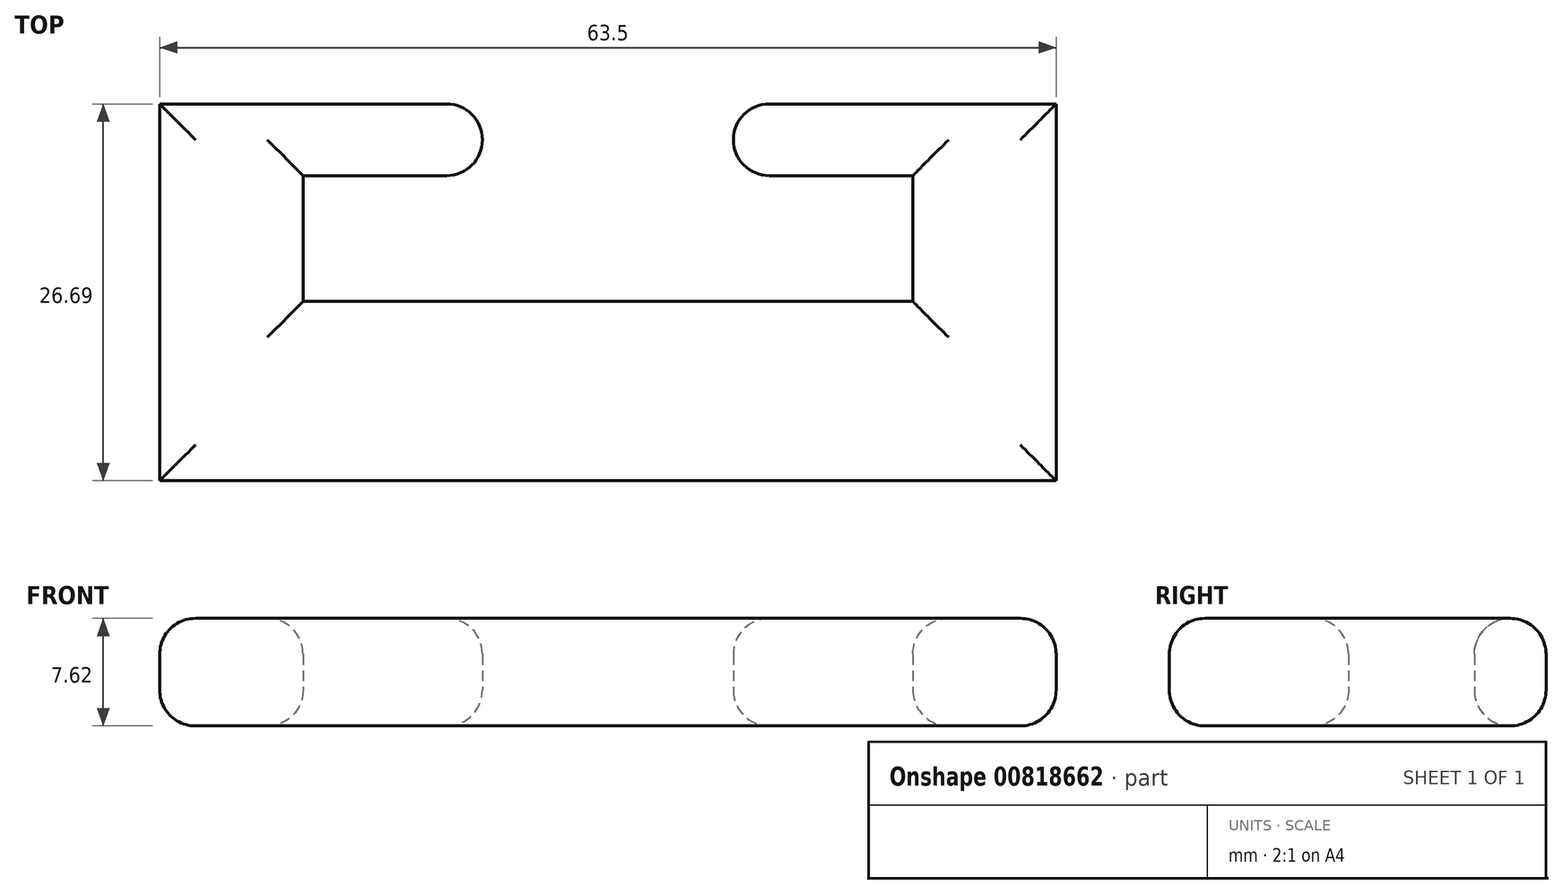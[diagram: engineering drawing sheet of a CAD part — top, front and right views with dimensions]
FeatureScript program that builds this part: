
annotation { "Feature Type Name" : "Feature", "Feature Type Description" : "" }
export const myFeature = defineFeature(function(context is Context, id is Id, definition is map)
    precondition{}
    {
        {
            var Q0;
            Q0=qCreatedBy(makeId("Top.planeOp"),FACE);
            var sketch = newSketch(context, id + "F0", { "sketchPlane" : qUnion([Q0])});
            skLineSegment(sketch, "E0.bottom", {"start": v(-30.15, 5.94) * mm, "end": v(33.35, 5.94) * mm});
            skLineSegment(sketch, "E0.top", {"start": v(-30.15, -6.76) * mm, "end": v(33.35, -6.76) * mm});
            skLineSegment(sketch, "E0.left", {"start": v(-30.15, 5.94) * mm, "end": v(-30.15, -6.76) * mm});
            skLineSegment(sketch, "E0.right", {"start": v(33.35, 5.94) * mm, "end": v(33.35, -6.76) * mm});
            skLineSegment(sketch, "E1.bottom", {"start": v(-30.15, 5.94) * mm, "end": v(-20, 5.94) * mm});
            skLineSegment(sketch, "E1.top", {"start": v(-30.15, 19.93) * mm, "end": v(-20, 19.93) * mm});
            skLineSegment(sketch, "E1.left", {"start": v(-30.15, 5.94) * mm, "end": v(-30.15, 19.93) * mm});
            skLineSegment(sketch, "E1.right", {"start": v(-20, 5.94) * mm, "end": v(-20, 19.93) * mm});
            skLineSegment(sketch, "E2.bottom", {"start": v(33.35, 5.94) * mm, "end": v(23.19, 5.94) * mm});
            skLineSegment(sketch, "E2.top", {"start": v(33.35, 19.93) * mm, "end": v(23.19, 19.93) * mm});
            skLineSegment(sketch, "E2.left", {"start": v(33.35, 5.94) * mm, "end": v(33.35, 19.93) * mm});
            skLineSegment(sketch, "E2.right", {"start": v(23.19, 5.94) * mm, "end": v(23.19, 19.93) * mm});
            skLineSegment(sketch, "E3.bottom", {"start": v(-20, 19.93) * mm, "end": v(-7.3, 19.93) * mm});
            skLineSegment(sketch, "E3.top", {"start": v(-20, 14.85) * mm, "end": v(-7.3, 14.85) * mm});
            skLineSegment(sketch, "E3.left", {"start": v(-20, 19.93) * mm, "end": v(-20, 14.85) * mm});
            skLineSegment(sketch, "E3.right", {"start": v(-7.3, 19.93) * mm, "end": v(-7.3, 14.85) * mm});
            skLineSegment(sketch, "E4.bottom", {"start": v(23.19, 19.93) * mm, "end": v(10.49, 19.93) * mm});
            skLineSegment(sketch, "E4.top", {"start": v(23.19, 14.85) * mm, "end": v(10.49, 14.85) * mm});
            skLineSegment(sketch, "E4.left", {"start": v(23.19, 19.93) * mm, "end": v(23.19, 14.85) * mm});
            skLineSegment(sketch, "E4.right", {"start": v(10.49, 19.93) * mm, "end": v(10.49, 14.85) * mm});
            skSolve(sketch);
        }
        {
            var Q0;
            Q0 = qSketchRegion(id + "F0", true);
            extrude(context, id + "F1", {"entities" : qUnion([Q0]), "depth" : 7.62 * mm, "offsetDistance" : 25.4 * mm});
        }
        {
            var Q0;
            Q0=makeQuery(id+"F1.opExtrude","CAP_EDGE",EDGE,{"disambiguationData":[OSD([sQuery(id+"F0.wireOp",EDGE,"E0.top")])],"isStart":false});
            var Q1;
            Q1=makeQuery(id+"F1.opExtrude","CAP_EDGE",EDGE,{"disambiguationData":[OSD([sQuery(id+"F0.wireOp",EDGE,"E0.bottom")])],"isStart":false});
            var Q2;
            Q2=makeQuery(id+"F1.opExtrude","CAP_EDGE",EDGE,{"disambiguationData":[OSD([sQuery(id+"F0.wireOp",EDGE,"E0.left"),sQuery(id+"F0.wireOp",EDGE,"E1.left")])],"isStart":false});
            var Q3;
            Q3=makeQuery(id+"F1.opExtrude","CAP_EDGE",EDGE,{"disambiguationData":[OSD([sQuery(id+"F0.wireOp",EDGE,"E0.right"),sQuery(id+"F0.wireOp",EDGE,"E2.left")])],"isStart":false});
            var Q4;
            Q4=makeQuery(id+"F1.opExtrude","CAP_EDGE",EDGE,{"disambiguationData":[OSD([sQuery(id+"F0.wireOp",EDGE,"E2.top"),sQuery(id+"F0.wireOp",EDGE,"E4.bottom")])],"isStart":false});
            var Q5;
            Q5=makeQuery(id+"F1.opExtrude","CAP_EDGE",EDGE,{"disambiguationData":[OSD([sQuery(id+"F0.wireOp",EDGE,"E1.top"),sQuery(id+"F0.wireOp",EDGE,"E3.bottom")])],"isStart":false});
            var Q6;
            Q6=makeQuery(id+"F1.opExtrude","CAP_EDGE",EDGE,{"disambiguationData":[OSD([sQuery(id+"F0.wireOp",EDGE,"E2.top"),sQuery(id+"F0.wireOp",EDGE,"E4.bottom")])],"isStart":true});
            var Q7;
            Q7=makeQuery(id+"F1.opExtrude","CAP_EDGE",EDGE,{"disambiguationData":[OSD([sQuery(id+"F0.wireOp",EDGE,"E2.right")])],"isStart":false});
            var Q8;
            Q8=makeQuery(id+"F1.opExtrude","CAP_EDGE",EDGE,{"disambiguationData":[OSD([sQuery(id+"F0.wireOp",EDGE,"E4.top")])],"isStart":false});
            var Q9;
            Q9=makeQuery(id+"F1.opExtrude","CAP_EDGE",EDGE,{"disambiguationData":[OSD([sQuery(id+"F0.wireOp",EDGE,"E3.top")])],"isStart":false});
            var Q10;
            Q10=makeQuery(id+"F1.opExtrude","CAP_EDGE",EDGE,{"disambiguationData":[OSD([sQuery(id+"F0.wireOp",EDGE,"E0.top")])],"isStart":true});
            var Q11;
            Q11=makeQuery(id+"F1.opExtrude","CAP_EDGE",EDGE,{"disambiguationData":[OSD([sQuery(id+"F0.wireOp",EDGE,"E0.left"),sQuery(id+"F0.wireOp",EDGE,"E1.left")])],"isStart":true});
            var Q12;
            Q12=makeQuery(id+"F1.opExtrude","CAP_EDGE",EDGE,{"disambiguationData":[OSD([sQuery(id+"F0.wireOp",EDGE,"E0.right"),sQuery(id+"F0.wireOp",EDGE,"E2.left")])],"isStart":true});
            var Q13;
            Q13=makeQuery(id+"F1.opExtrude","SWEPT_EDGE",EDGE,{"disambiguationData":[OSD([sQuery(id+"F0.wireOp",EDGE,"E4.top"),sQuery(id+"F0.wireOp",EDGE,"E4.right")])]});
            var Q14;
            Q14=makeQuery(id+"F1.opExtrude","SWEPT_EDGE",EDGE,{"disambiguationData":[OSD([sQuery(id+"F0.wireOp",EDGE,"E4.bottom"),sQuery(id+"F0.wireOp",EDGE,"E4.right")])]});
            var Q15;
            Q15=makeQuery(id+"F1.opExtrude","SWEPT_EDGE",EDGE,{"disambiguationData":[OSD([sQuery(id+"F0.wireOp",EDGE,"E3.top"),sQuery(id+"F0.wireOp",EDGE,"E3.right")])]});
            var Q16;
            Q16=makeQuery(id+"F1.opExtrude","SWEPT_EDGE",EDGE,{"disambiguationData":[OSD([sQuery(id+"F0.wireOp",EDGE,"E3.bottom"),sQuery(id+"F0.wireOp",EDGE,"E3.right")])]});
            var Q17;
            Q17=makeQuery(id+"F1.opExtrude","CAP_EDGE",EDGE,{"disambiguationData":[OSD([sQuery(id+"F0.wireOp",EDGE,"E1.right")])],"isStart":false});
            var Q18;
            Q18=makeQuery(id+"F1.opExtrude","CAP_EDGE",EDGE,{"disambiguationData":[OSD([sQuery(id+"F0.wireOp",EDGE,"E0.bottom")])],"isStart":true});
            var Q19;
            Q19=makeQuery(id+"F1.opExtrude","CAP_EDGE",EDGE,{"disambiguationData":[OSD([sQuery(id+"F0.wireOp",EDGE,"E1.right")])],"isStart":true});
            var Q20;
            Q20=makeQuery(id+"F1.opExtrude","CAP_EDGE",EDGE,{"disambiguationData":[OSD([sQuery(id+"F0.wireOp",EDGE,"E4.top")])],"isStart":true});
            var Q21;
            Q21=makeQuery(id+"F1.opExtrude","CAP_EDGE",EDGE,{"disambiguationData":[OSD([sQuery(id+"F0.wireOp",EDGE,"E2.right")])],"isStart":true});
            var Q22;
            Q22=makeQuery(id+"F1.opExtrude","CAP_EDGE",EDGE,{"disambiguationData":[OSD([sQuery(id+"F0.wireOp",EDGE,"E3.top")])],"isStart":true});
            var Q23;
            Q23=makeQuery(id+"F1.opExtrude","CAP_EDGE",EDGE,{"disambiguationData":[OSD([sQuery(id+"F0.wireOp",EDGE,"E4.right")])],"isStart":true});
            var Q24;
            Q24=makeQuery(id+"F1.opExtrude","CAP_EDGE",EDGE,{"disambiguationData":[OSD([sQuery(id+"F0.wireOp",EDGE,"E3.right")])],"isStart":true});
            var Q25;
            Q25=makeQuery(id+"F1.opExtrude","CAP_EDGE",EDGE,{"disambiguationData":[OSD([sQuery(id+"F0.wireOp",EDGE,"E1.top"),sQuery(id+"F0.wireOp",EDGE,"E3.bottom")])],"isStart":true});
            var Q26;
            Q26=makeQuery(id+"F1.opExtrude","CAP_EDGE",EDGE,{"disambiguationData":[OSD([sQuery(id+"F0.wireOp",EDGE,"E4.right")])],"isStart":false});
            var Q27;
            Q27=makeQuery(id+"F1.opExtrude","CAP_EDGE",EDGE,{"disambiguationData":[OSD([sQuery(id+"F0.wireOp",EDGE,"E3.right")])],"isStart":false});
            fillet(context, id + "F2", {"entities" : qUnion([Q0, Q1, Q2, Q3, Q4, Q5, Q6, Q7, Q8, Q9, Q10, Q11, Q12, Q13, Q14, Q15, Q16, Q17, Q18, Q19, Q20, Q21, Q22, Q23, Q24, Q25, Q26, Q27]), "radius" : 2.54 * mm, "tangentPropagation" : true, "allowEdgeOverflow" : false});
        }
    });
